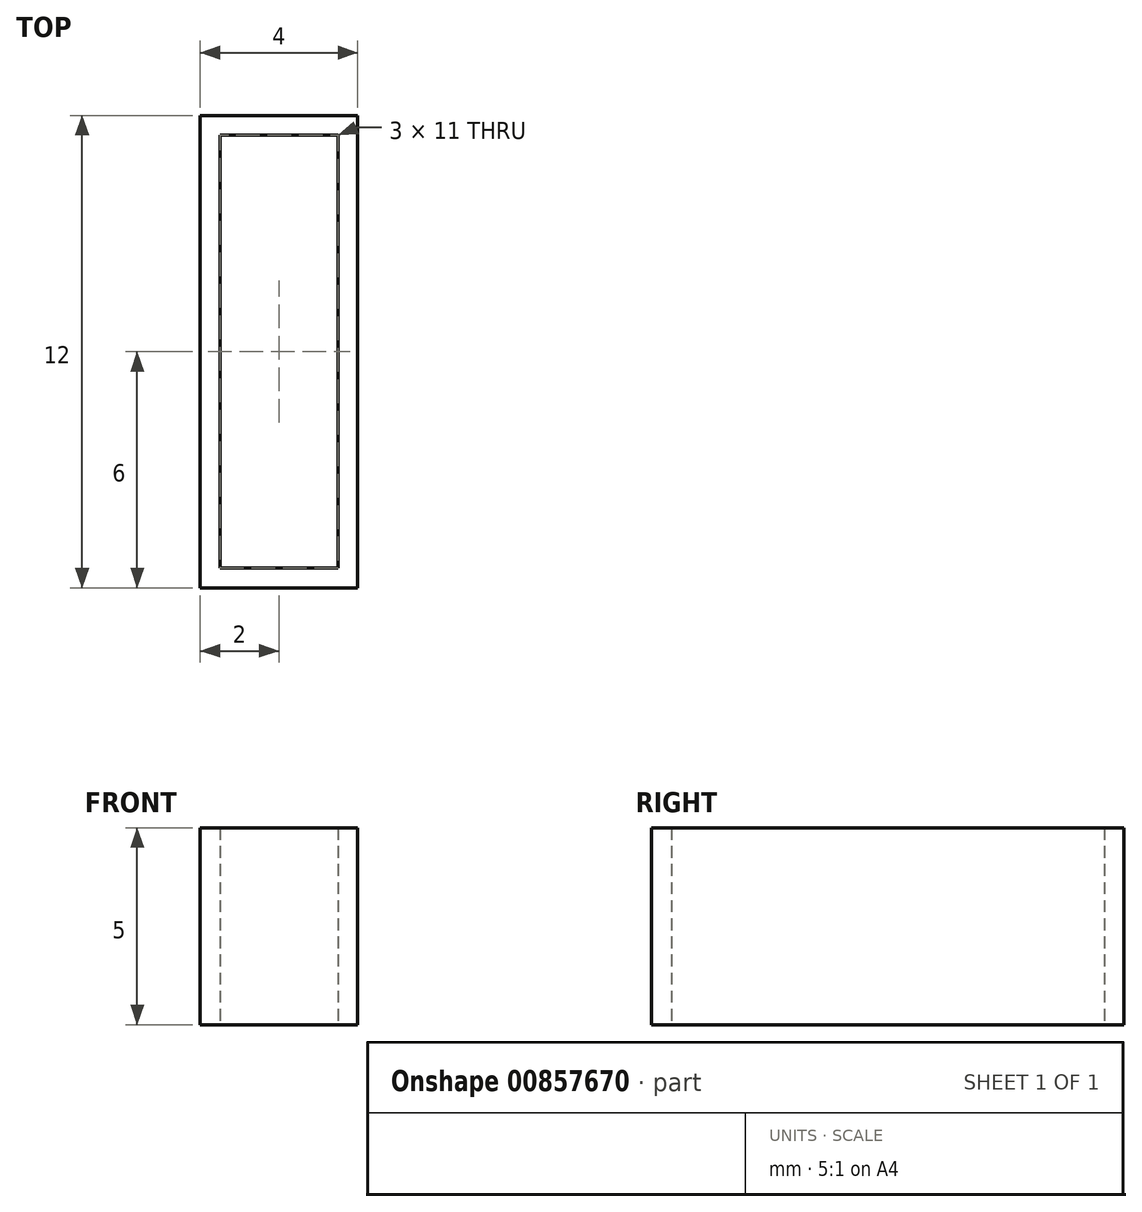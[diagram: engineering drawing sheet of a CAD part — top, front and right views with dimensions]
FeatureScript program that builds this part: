
annotation { "Feature Type Name" : "Feature", "Feature Type Description" : "" }
export const myFeature = defineFeature(function(context is Context, id is Id, definition is map)
    precondition{}
    {
        {
            var Q0;
            Q0=qCreatedBy(makeId("Top.planeOp"),FACE);
            var sketch = newSketch(context, id + "F0", { "sketchPlane" : qUnion([Q0])});
            skLineSegment(sketch, "E0.bottom", {"start": v(1.5, 5.5) * mm, "end": v(-1.5, 5.5) * mm});
            skLineSegment(sketch, "E0.top", {"start": v(1.5, -5.5) * mm, "end": v(-1.5, -5.5) * mm});
            skLineSegment(sketch, "E0.left", {"start": v(1.5, 5.5) * mm, "end": v(1.5, -5.5) * mm});
            skLineSegment(sketch, "E0.right", {"start": v(-1.5, 5.5) * mm, "end": v(-1.5, -5.5) * mm});
            skPoint(sketch, "E0.middle", {"position": v(0, 0) * mm});
            skLineSegment(sketch, "E1.bottom", {"start": v(2, -6) * mm, "end": v(-2, -6) * mm});
            skLineSegment(sketch, "E1.top", {"start": v(2, 6) * mm, "end": v(-2, 6) * mm});
            skLineSegment(sketch, "E1.left", {"start": v(2, -6) * mm, "end": v(2, 6) * mm});
            skLineSegment(sketch, "E1.right", {"start": v(-2, -6) * mm, "end": v(-2, 6) * mm});
            skSolve(sketch);
        }
        {
            var Q0;
            Q0=makeQuery(id+"F0.imprint","IMPRINT",FACE,{"disambiguationData":[TD([[makeQuery(id+"F0.imprint","IMPRINT",EDGE,{"derivedFrom":sQuery(id+"F0.wireOp",EDGE,"E0.bottom")}),-1.0]])]});
            extrude(context, id + "F1", {"entities" : qUnion([Q0]), "endBound" : BoundingType.SYMMETRIC, "depth" : 5 * mm, "offsetDistance" : 25 * mm});
        }
    });
